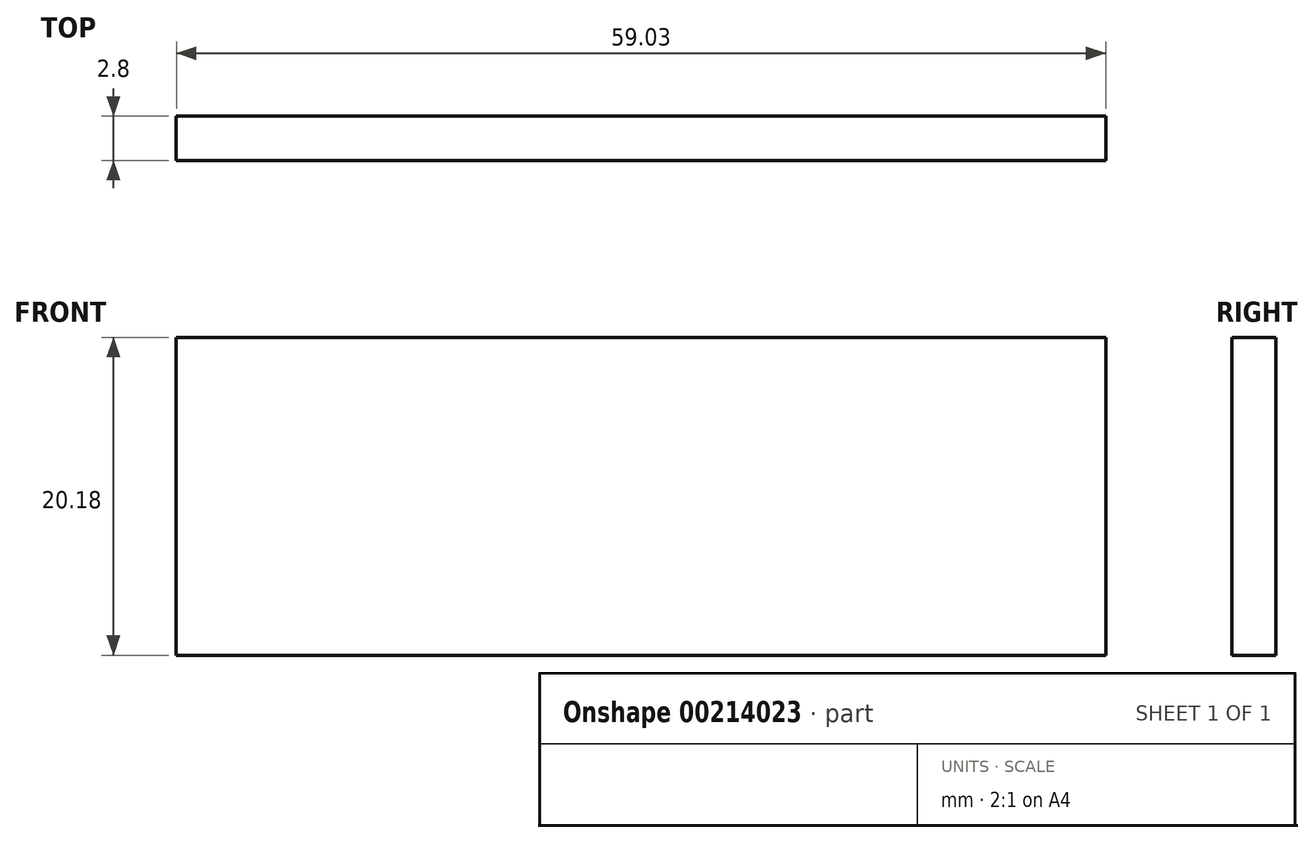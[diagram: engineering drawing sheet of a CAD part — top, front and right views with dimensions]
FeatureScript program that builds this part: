
annotation { "Feature Type Name" : "Feature", "Feature Type Description" : "" }
export const myFeature = defineFeature(function(context is Context, id is Id, definition is map)
    precondition{}
    {
        {
            var Q0;
            Q0=qCreatedBy(makeId("Front.planeOp"),FACE);
            var sketch = newSketch(context, id + "F0", { "sketchPlane" : qUnion([Q0])});
            skLineSegment(sketch, "E0.bottom", {"start": v(0, 0) * mm, "end": v(-59.03, 0) * mm});
            skLineSegment(sketch, "E0.top", {"start": v(0, -20.18) * mm, "end": v(-59.03, -20.18) * mm});
            skLineSegment(sketch, "E0.left", {"start": v(0, 0) * mm, "end": v(0, -20.18) * mm});
            skLineSegment(sketch, "E0.right", {"start": v(-59.03, 0) * mm, "end": v(-59.03, -20.18) * mm});
            skSolve(sketch);
        }
        {
            var Q0;
            Q0=makeQuery(id+"F0.imprint","IMPRINT",FACE,{"disambiguationData":[TD([[makeQuery(id+"F0.imprint","IMPRINT",EDGE,{"derivedFrom":sQuery(id+"F0.wireOp",EDGE,"E0.bottom")}),1.0]])]});
            extrude(context, id + "F1", {"entities" : qUnion([Q0]), "depth" : 2.8 * mm});
        }
        {
            var Q0;
            Q0=qCreatedBy(makeId("Front.planeOp"),FACE);
            var sketch = newSketch(context, id + "F2", { "sketchPlane" : qUnion([Q0])});
            skCircle(sketch, "E1", {"center": v(-52.38, -9.51) * mm, "radius": 4.6 * mm});
            skCircle(sketch, "E2", {"center": v(-32.05, -9.51) * mm, "radius": 4.96 * mm});
            skSolve(sketch);
        }
        {
            var Q0;
            Q0=sQuery(id+"F2.wireOp",EDGE,"E1");
            extrude(context, id + "F3", {"bodyType" : ToolBodyType.SURFACE, "surfaceEntities" : qUnion([Q0]), "depth" : 13.2 * mm});
        }
    });
